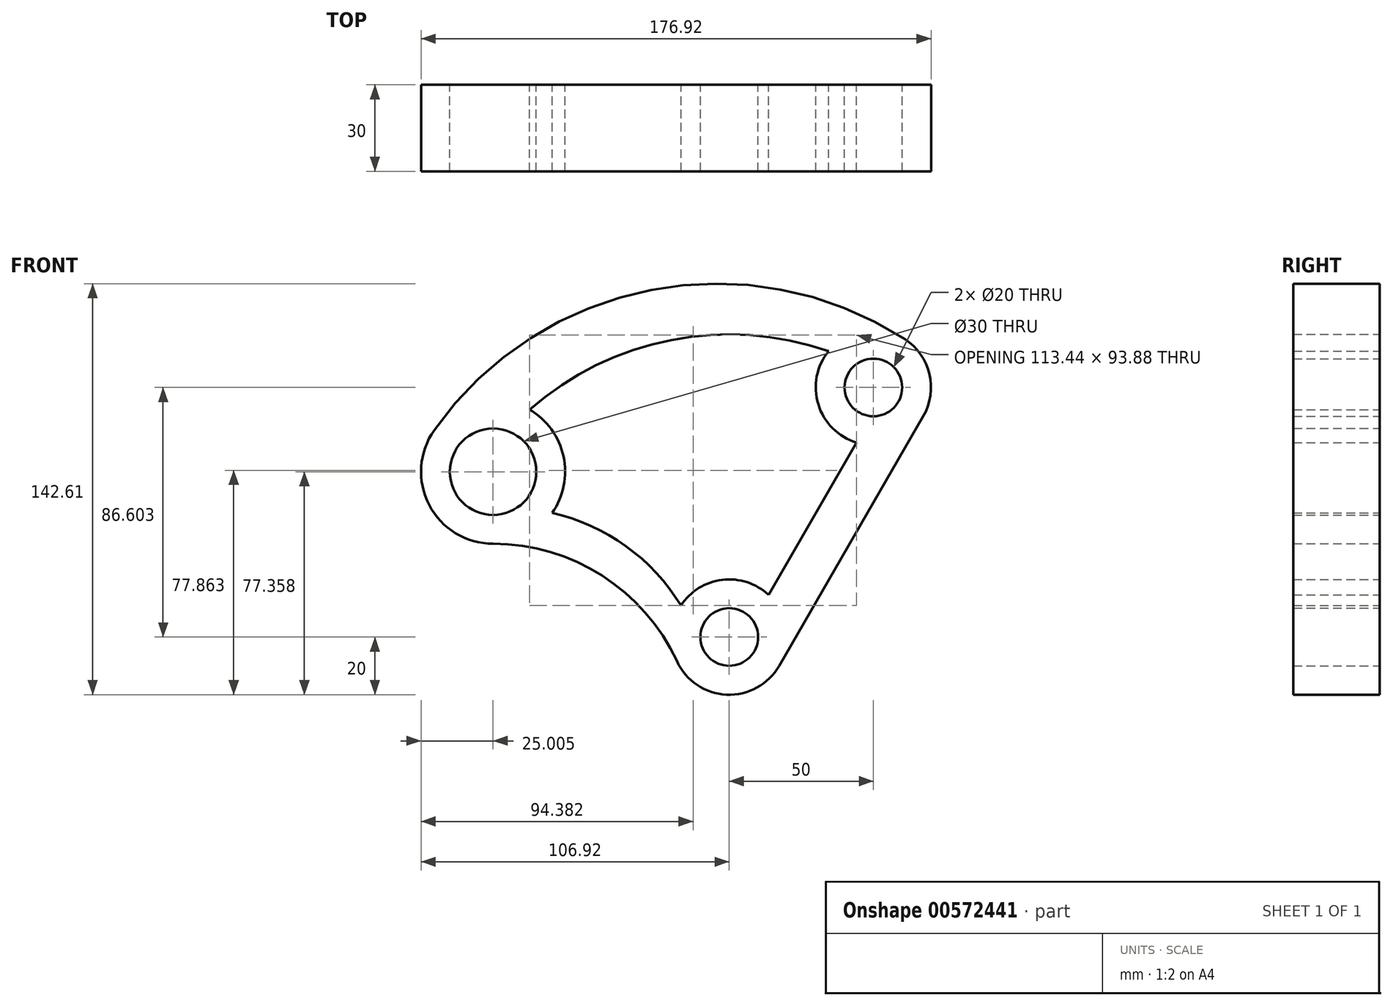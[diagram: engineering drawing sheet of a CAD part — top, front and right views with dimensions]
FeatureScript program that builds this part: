
annotation { "Feature Type Name" : "Feature", "Feature Type Description" : "" }
export const myFeature = defineFeature(function(context is Context, id is Id, definition is map)
    precondition{}
    {
        {
            var Q0;
            Q0=qCreatedBy(makeId("Front.planeOp"),FACE);
            var sketch = newSketch(context, id + "F0", { "sketchPlane" : qUnion([Q0])});
            skCircle(sketch, "E0", {"center": v(0, 0) * mm, "radius": 10 * mm});
            skCircle(sketch, "E1", {"center": v(-81.92, 57.36) * mm, "radius": 15 * mm});
            skCircle(sketch, "E2", {"center": v(50, 86.6) * mm, "radius": 10 * mm});
            skArc(sketch, "E3", {"start": v(-18.15, -8.4) * mm, "mid": v(-0.9, -19.98) * mm, "end": v(17.32, -10) * mm});
            skArc(sketch, "E4", {"start": v(-102.35, 71.76) * mm, "mid": v(-104.1, 45.85) * mm, "end": v(-81.92, 32.36) * mm});
            skArc(sketch, "E5", {"start": v(34.45, 99.19) * mm, "mid": v(30.88, 80.74) * mm, "end": v(44.18, 67.47) * mm});
            skLineSegment(sketch, "E6", {"start": v(-81.92, 57.36) * mm, "end": v(0, 0) * mm, "construction": true});
            skLineSegment(sketch, "E7", {"start": v(50, 86.6) * mm, "end": v(0, 0) * mm, "construction": true});
            skLineSegment(sketch, "E8", {"start": v(0, 0) * mm, "end": v(0, 134.72) * mm, "construction": true});
            skArc(sketch, "E9", {"start": v(55.43, 95) * mm, "mid": v(-25.2, 110.6) * mm, "end": v(-94.17, 66) * mm, "construction": true});
            skArc(sketch, "E10", {"start": v(34.45, 99.19) * mm, "mid": v(-20.14, 103.05) * mm, "end": v(-69.26, 78.92) * mm});
            skArc(sketch, "E11", {"start": v(60.85, 103.4) * mm, "mid": v(-27.11, 120.42) * mm, "end": v(-102.35, 71.76) * mm});
            skLineSegment(sketch, "E12", {"start": v(67.32, 76.6) * mm, "end": v(17.32, -10) * mm});
            skLineSegment(sketch, "E13", {"start": v(13.66, 14.6) * mm, "end": v(44.18, 67.47) * mm});
            skArc(sketch, "E14", {"start": v(-18.15, -8.4) * mm, "mid": v(-44.08, 21.3) * mm, "end": v(-81.92, 32.36) * mm});
            skArc(sketch, "E15", {"start": v(-16.75, 10.92) * mm, "mid": v(-35.82, 31.53) * mm, "end": v(-61.44, 43.02) * mm});
            skArc(sketch, "E16.trimOffspring", {"start": v(-61.44, 43.02) * mm, "mid": v(-57.49, 62.68) * mm, "end": v(-69.26, 78.92) * mm});
            skArc(sketch, "E17.trimOffspring", {"start": v(13.66, 14.6) * mm, "mid": v(-2.4, 19.86) * mm, "end": v(-16.75, 10.92) * mm});
            skArc(sketch, "E18.trimOffspring", {"start": v(67.32, 76.6) * mm, "mid": v(69.44, 91.3) * mm, "end": v(60.85, 103.4) * mm});
            skSolve(sketch);
        }
        {
            var Q0;
            Q0 = qSketchRegion(id + "F0", true);
            extrude(context, id + "F1", {"entities" : qUnion([Q0]), "depth" : 30 * mm, "offsetDistance" : 25 * mm});
        }
    });
